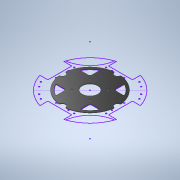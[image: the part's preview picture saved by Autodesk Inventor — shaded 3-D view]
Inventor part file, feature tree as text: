
AUTODESK INVENTOR PART (.ipt)
format: ipt  version: 2020 (Build 240168000, 168)  size: 237,568 bytes
history: native  units: mm
features: sketch x5, extrude x2, other x1, fillet x1
ambient origin geometry x8: Origin, YZ Plane, XZ Plane, XY Plane, X Axis, Y Axis, Z Axis, Center Point
bodies: Body1 (feature_tree)
feature tree (9):
  other  "Твердое тело1"
  sketch  "Эскиз1"
  sketch  "Эскиз4"
  extrude  "Выдавливание1"  Depth=8.0mm
  fillet  "Сопряжение1"  Radius=40.0mm
  extrude  "Выдавливание2"  Depth=112.2mm
  sketch  "Эскиз6"
  sketch  "Эскиз2"
  sketch  "Эскиз5"
